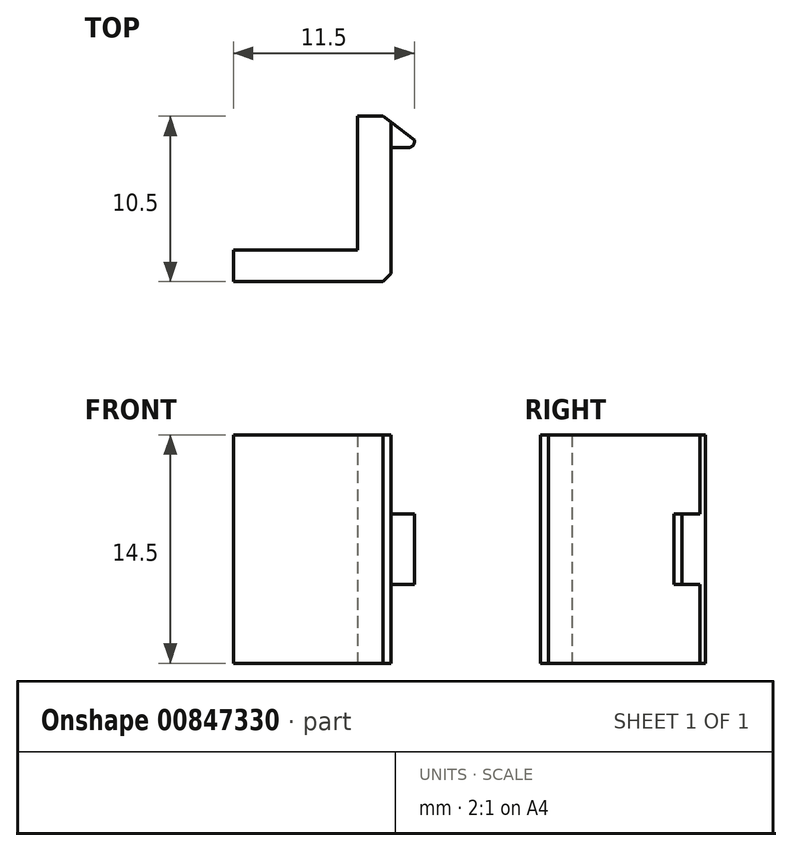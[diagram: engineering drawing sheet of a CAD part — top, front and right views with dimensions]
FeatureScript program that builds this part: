
annotation { "Feature Type Name" : "Feature", "Feature Type Description" : "" }
export const myFeature = defineFeature(function(context is Context, id is Id, definition is map)
    precondition{}
    {
        {
            var Q0;
            Q0=qCreatedBy(makeId("Top.planeOp"),FACE);
            var sketch = newSketch(context, id + "F0", { "sketchPlane" : qUnion([Q0])});
            skLineSegment(sketch, "E0", {"start": v(0, 0) * mm, "end": v(10, 0) * mm});
            skLineSegment(sketch, "E1", {"start": v(10, 0) * mm, "end": v(10, 8.5) * mm});
            skLineSegment(sketch, "E2", {"start": v(10, 8.5) * mm, "end": v(11.5, 8.5) * mm});
            skLineSegment(sketch, "E3", {"start": v(11.5, 8.5) * mm, "end": v(11.5, 10.5) * mm});
            skLineSegment(sketch, "E4", {"start": v(11.5, 10.5) * mm, "end": v(7.9, 10.5) * mm});
            skLineSegment(sketch, "E5", {"start": v(7.9, 10.5) * mm, "end": v(7.9, 2) * mm});
            skLineSegment(sketch, "E6", {"start": v(7.9, 2) * mm, "end": v(0, 2) * mm});
            skLineSegment(sketch, "E7", {"start": v(0, 2) * mm, "end": v(0, 0) * mm});
            skLineSegment(sketch, "E8", {"start": v(10, 8.5) * mm, "end": v(10, 10.5) * mm});
            skSolve(sketch);
        }
        {
            var Q0;
            Q0=makeQuery(id+"F0.imprint","IMPRINT",FACE,{"disambiguationData":[TD([[makeQuery(id+"F0.imprint","IMPRINT",EDGE,{"derivedFrom":sQuery(id+"F0.wireOp",EDGE,"E0")}),1.0]])]});
            extrude(context, id + "F1", {"entities" : qUnion([Q0]), "depth" : 14.5 * mm, "offsetDistance" : 25 * mm});
        }
        {
            var Q0;
            Q0=makeQuery(id+"F0.imprint","IMPRINT",FACE,{"disambiguationData":[TD([[makeQuery(id+"F0.imprint","IMPRINT",EDGE,{"derivedFrom":sQuery(id+"F0.wireOp",EDGE,"E2")}),1.0]])]});
            extrude(context, id + "F2", {"entities" : qUnion([Q0]), "operationType" : NewBodyOperationType.ADD, "depth" : 9.5 * mm, "offsetDistance" : 25 * mm, "hasSecondDirection" : true, "secondDirectionOppositeDirection" : false, "secondDirectionDepth" : 5 * mm});
        }
        {
            var Q0;
            Q0=makeQuery(id+"F1.opExtrude","SWEPT_EDGE",EDGE,{"disambiguationData":[OSD([sQuery(id+"F0.wireOp",EDGE,"E0"),sQuery(id+"F0.wireOp",EDGE,"E1")])]});
            chamfer(context, id + "F3", {"entities" : qUnion([Q0]), "width" : .5 * mm, "tangentPropagation" : true});
        }
        {
            var Q0;
            Q0=makeQuery(id+"F2.opExtrude","SWEPT_EDGE",EDGE,{"disambiguationData":[OSD([sQuery(id+"F0.wireOp",EDGE,"E3"),sQuery(id+"F0.wireOp",EDGE,"E4")])]});
            chamfer(context, id + "F4", {"entities" : qUnion([Q0]), "chamferType" : ChamferType.TWO_OFFSETS, "width1" : 2 * mm, "oppositeDirection" : false, "width2" : 1.5 * mm});
        }
        {
            var Q0;
            Q0=makeQuery(id+"F2.opExtrude","SWEPT_EDGE",EDGE,{"disambiguationData":[OSD([sQuery(id+"F0.wireOp",EDGE,"E2"),sQuery(id+"F0.wireOp",EDGE,"E3")])]});
            fillet(context, id + "F5", {"entities" : qUnion([Q0]), "radius" : .4 * mm, "tangentPropagation" : true, "allowEdgeOverflow" : false});
        }
    });
